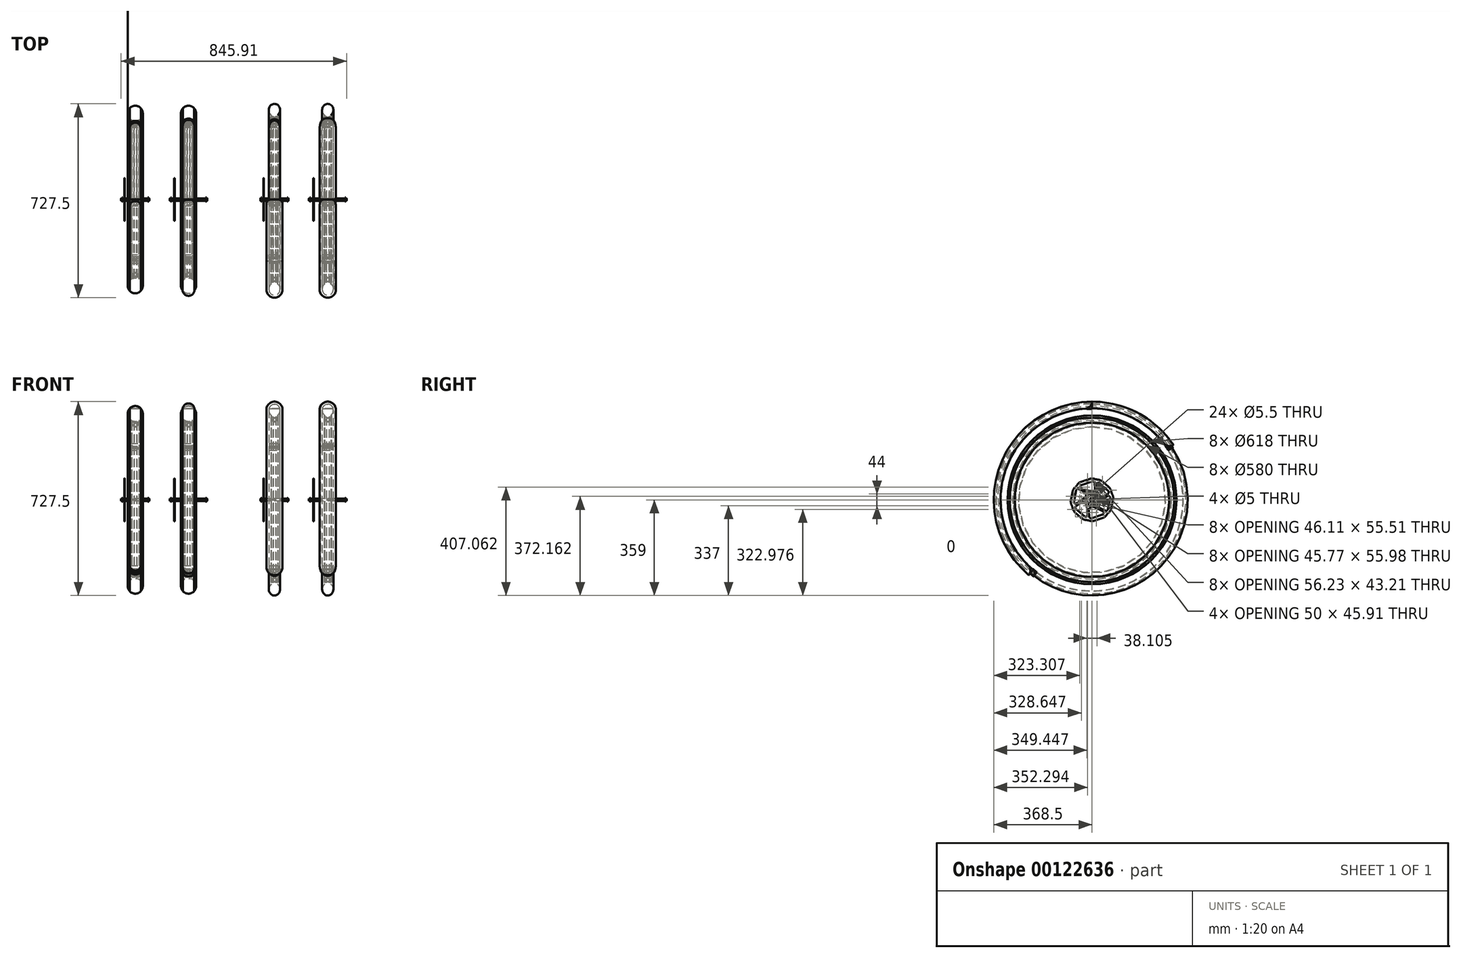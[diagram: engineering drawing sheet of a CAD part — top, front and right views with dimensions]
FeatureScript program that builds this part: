
annotation { "Feature Type Name" : "Feature", "Feature Type Description" : "" }
export const myFeature = defineFeature(function(context is Context, id is Id, definition is map)
    precondition{}
    {
        {
            var Q0;
            Q0=qCreatedBy(makeId("Front.planeOp"),FACE);
            var sketch = newSketch(context, id + "F0", { "sketchPlane" : qUnion([Q0])});
            skLineSegment(sketch, "E0.0", {"start": v(0, 313.27) * mm, "end": v(0, 0) * mm, "construction": true});
            skPoint(sketch, "E1.0", {"position": v(0, 0) * mm});
            skEllipticalArc(sketch, "E2", {});
            skLineSegment(sketch, "E3", {"start": v(-11.5, 309) * mm, "end": v(-5.5, 309) * mm});
            skArc(sketch, "E4", {"start": v(-5.5, 309) * mm, "mid": v(0, 306.5) * mm, "end": v(5.5, 309) * mm});
            skArc(sketch, "E5", {"start": v(-8.42, 300.83) * mm, "mid": v(0, 295) * mm, "end": v(8.42, 300.83) * mm});
            skLineSegment(sketch, "E6", {"start": v(-8.42, 300.83) * mm, "end": v(-11.5, 309) * mm});
            skLineSegment(sketch, "E7", {"start": v(5.5, 309) * mm, "end": v(11.5, 309) * mm});
            skLineSegment(sketch, "E8", {"start": v(11.5, 309) * mm, "end": v(8.42, 300.83) * mm});
            skLineSegment(sketch, "E9.1", {"start": v(4.5, 311) * mm, "end": v(11.5, 311) * mm});
            skArc(sketch, "E9.3", {"start": v(-4.5, 311) * mm, "mid": v(0, 308.5) * mm, "end": v(4.5, 311) * mm});
            skLineSegment(sketch, "E10", {"start": v(-11.5, 311) * mm, "end": v(-11.5, 317) * mm});
            skLineSegment(sketch, "E11", {"start": v(11.5, 311) * mm, "end": v(11.5, 317) * mm});
            skLineSegment(sketch, "E12.0", {"start": v(13.5, 308.64) * mm, "end": v(13.5, 317) * mm});
            skLineSegment(sketch, "E12.1", {"start": v(-13.5, 308.64) * mm, "end": v(-13.5, 317) * mm});
            skLineSegment(sketch, "E12.2", {"start": v(-10.3, 300.12) * mm, "end": v(-13.5, 308.64) * mm});
            skArc(sketch, "E12.3", {"start": v(-10.3, 300.12) * mm, "mid": v(0, 293) * mm, "end": v(10.3, 300.12) * mm});
            skLineSegment(sketch, "E12.4", {"start": v(13.5, 308.64) * mm, "end": v(10.3, 300.12) * mm});
            skLineSegment(sketch, "E13.trimOffspring", {"start": v(-11.5, 311) * mm, "end": v(-4.5, 311) * mm});
            skPoint(sketch, "E14", {"position": v(0, 308.5) * mm});
            skLineSegment(sketch, "E15", {"start": v(-11.5, 317) * mm, "end": v(-13.5, 317) * mm});
            skLineSegment(sketch, "E16", {"start": v(11.5, 317) * mm, "end": v(13.5, 317) * mm});
            skPoint(sketch, "E17", {"position": v(0, 295) * mm});
            skLineSegment(sketch, "E18", {"start": v(-21, 336.13) * mm, "end": v(21, 336.13) * mm, "construction": true});
            skPoint(sketch, "E19.orphan", {"position": v(0, 359) * mm});
            skLineSegment(sketch, "E20", {"start": v(-50, 7.5) * mm, "end": v(-50, 4.5) * mm});
            skPoint(sketch, "E21", {"position": v(53, 0) * mm});
            skPoint(sketch, "E22", {"position": v(-50, -7.5) * mm});
            skPoint(sketch, "E23", {"position": v(-47, 7.5) * mm});
            skPoint(sketch, "E24", {"position": v(-47, 4.5) * mm});
            skLineSegment(sketch, "E25", {"start": v(-50, 7.5) * mm, "end": v(-47, 7.5) * mm});
            skLineSegment(sketch, "E26", {"start": v(-47, 4.5) * mm, "end": v(-47, 7.5) * mm});
            skPoint(sketch, "E27.orphan", {"position": v(-50, 4.5) * mm});
            skLineSegment(sketch, "E28", {"start": v(-50, 4.5) * mm, "end": v(-53, 4.5) * mm});
            skLineSegment(sketch, "E29", {"start": v(-53, 4.5) * mm, "end": v(-53, 2.5) * mm});
            skLineSegment(sketch, "E30", {"start": v(0, 0) * mm, "end": v(53, 0) * mm, "construction": true});
            skPoint(sketch, "E31", {"position": v(-53, 2.5) * mm});
            skPoint(sketch, "E32.MirrorP", {"position": v(-53, -2.5) * mm});
            skPoint(sketch, "E33", {"position": v(-53, 4.5) * mm});
            skPoint(sketch, "E34.MirrorP", {"position": v(-53, -4.5) * mm});
            skLineSegment(sketch, "E35", {"start": v(-53, 2.5) * mm, "end": v(53, 2.5) * mm});
            skLineSegment(sketch, "E36", {"start": v(47, 4.5) * mm, "end": v(-47, 4.5) * mm});
            skArc(sketch, "E37", {"start": v(28.52, 343.23) * mm, "mid": v(0, 367) * mm, "end": v(-28.52, 343.23) * mm});
            skArc(sketch, "E38.0", {"start": v(30, 343.5) * mm, "mid": v(0, 368.5) * mm, "end": v(-30, 343.5) * mm});
            skLineSegment(sketch, "E39", {"start": v(-28.52, 343.23) * mm, "end": v(-30, 343.5) * mm});
            skLineSegment(sketch, "E40", {"start": v(28.52, 343.23) * mm, "end": v(30, 343.5) * mm});
            skPoint(sketch, "E41", {"position": v(0, 368.5) * mm});
            skPoint(sketch, "E42", {"position": v(0, 367) * mm});
            skPoint(sketch, "E43", {"position": v(-50, 7.5) * mm});
            skPoint(sketch, "E44.MirrorP", {"position": v(47, 7.5) * mm});
            skPoint(sketch, "E45.MirrorP", {"position": v(50, 7.5) * mm});
            skPoint(sketch, "E46.MirrorP", {"position": v(50, 4.5) * mm});
            skPoint(sketch, "E47.MirrorP", {"position": v(53, 4.5) * mm});
            skLineSegment(sketch, "E48", {"start": v(47, 4.5) * mm, "end": v(47, 7.5) * mm});
            skLineSegment(sketch, "E49", {"start": v(50, 7.5) * mm, "end": v(50, 4.5) * mm});
            skLineSegment(sketch, "E50", {"start": v(50, 7.5) * mm, "end": v(47, 7.5) * mm});
            skLineSegment(sketch, "E51", {"start": v(50, 4.5) * mm, "end": v(53, 4.5) * mm});
            skLineSegment(sketch, "E52", {"start": v(53, 4.5) * mm, "end": v(53, 2.5) * mm});
            skLineSegment(sketch, "E53.0", {"start": v(-522.41, 294.8) * mm, "end": v(-522.41, 0) * mm, "construction": true});
            skLineSegment(sketch, "E54", {"start": v(-535.91, 290) * mm, "end": v(-527.91, 290) * mm});
            skArc(sketch, "E55", {"start": v(-527.91, 290) * mm, "mid": v(-522.41, 287.5) * mm, "end": v(-516.91, 290) * mm});
            skArc(sketch, "E56", {"start": v(-530.13, 280.37) * mm, "mid": v(-522.41, 276) * mm, "end": v(-514.7, 280.37) * mm});
            skLineSegment(sketch, "E57", {"start": v(-530.13, 280.37) * mm, "end": v(-535.91, 290) * mm});
            skLineSegment(sketch, "E58", {"start": v(-516.91, 290) * mm, "end": v(-508.91, 290) * mm});
            skLineSegment(sketch, "E59", {"start": v(-508.91, 290) * mm, "end": v(-514.7, 280.37) * mm});
            skLineSegment(sketch, "E60.1", {"start": v(-517.91, 292) * mm, "end": v(-508.91, 292) * mm});
            skArc(sketch, "E60.3", {"start": v(-526.91, 292) * mm, "mid": v(-522.41, 289.5) * mm, "end": v(-517.91, 292) * mm});
            skLineSegment(sketch, "E61", {"start": v(-535.91, 292) * mm, "end": v(-535.91, 298) * mm});
            skLineSegment(sketch, "E62", {"start": v(-508.91, 292) * mm, "end": v(-508.91, 298) * mm});
            skLineSegment(sketch, "E63.0", {"start": v(-506.91, 289.45) * mm, "end": v(-506.91, 298) * mm});
            skLineSegment(sketch, "E63.1", {"start": v(-537.91, 289.45) * mm, "end": v(-537.91, 298) * mm});
            skLineSegment(sketch, "E63.2", {"start": v(-531.85, 279.34) * mm, "end": v(-537.91, 289.45) * mm});
            skArc(sketch, "E63.3", {"start": v(-531.85, 279.34) * mm, "mid": v(-522.41, 274) * mm, "end": v(-512.98, 279.34) * mm});
            skLineSegment(sketch, "E63.4", {"start": v(-506.91, 289.45) * mm, "end": v(-512.98, 279.34) * mm});
            skLineSegment(sketch, "E64.trimOffspring", {"start": v(-535.91, 292) * mm, "end": v(-526.91, 292) * mm});
            skPoint(sketch, "E65", {"position": v(-522.41, 289.5) * mm});
            skLineSegment(sketch, "E66", {"start": v(-535.91, 298) * mm, "end": v(-537.91, 298) * mm});
            skLineSegment(sketch, "E67", {"start": v(-508.91, 298) * mm, "end": v(-506.91, 298) * mm});
            skPoint(sketch, "E68", {"position": v(-522.41, 276) * mm});
            skPoint(sketch, "E69.orphan", {"position": v(-522.41, 352) * mm});
            skLineSegment(sketch, "E70", {"start": v(-522.41, 0) * mm, "end": v(-522.41, 0) * mm});
            skArc(sketch, "E71", {"start": v(-501.4, 341.32) * mm, "mid": v(-522.41, 360) * mm, "end": v(-543.42, 341.32) * mm});
            skArc(sketch, "E72.0", {"start": v(-499.91, 341.5) * mm, "mid": v(-522.41, 361.5) * mm, "end": v(-544.91, 341.5) * mm});
            skLineSegment(sketch, "E73", {"start": v(-543.42, 341.32) * mm, "end": v(-544.91, 341.5) * mm});
            skLineSegment(sketch, "E74", {"start": v(-501.4, 341.32) * mm, "end": v(-499.91, 341.5) * mm});
            skPoint(sketch, "E75", {"position": v(-522.41, 361.5) * mm});
            skPoint(sketch, "E76", {"position": v(-522.41, 360) * mm});
            skPoint(sketch, "E77.1.0.0", {"position": v(200, 367) * mm});
            skArc(sketch, "E77.1.0.1", {"start": v(230, 343.5) * mm, "mid": v(200, 368.5) * mm, "end": v(170, 343.5) * mm});
            skArc(sketch, "E77.1.0.2", {"start": v(228.52, 343.23) * mm, "mid": v(200, 367) * mm, "end": v(171.48, 343.23) * mm});
            skPoint(sketch, "E77.1.0.3", {"position": v(200, 368.5) * mm});
            skLineSegment(sketch, "E77.1.0.4", {"start": v(228.52, 343.23) * mm, "end": v(230, 343.5) * mm});
            skLineSegment(sketch, "E77.1.0.5", {"start": v(171.48, 343.23) * mm, "end": v(170, 343.5) * mm});
            skLineSegment(sketch, "E77.direction1", {"start": v(170, 343.5) * mm, "end": v(-30, 343.5) * mm, "construction": true});
            skArc(sketch, "E78.1.0.0", {"start": v(-301.4, 341.32) * mm, "mid": v(-322.41, 360) * mm, "end": v(-343.42, 341.32) * mm});
            skArc(sketch, "E78.1.0.1", {"start": v(-299.91, 341.5) * mm, "mid": v(-322.41, 361.5) * mm, "end": v(-344.91, 341.5) * mm});
            skPoint(sketch, "E78.1.0.2", {"position": v(-322.41, 360) * mm});
            skPoint(sketch, "E78.1.0.3", {"position": v(-322.41, 361.5) * mm});
            skLineSegment(sketch, "E78.1.0.4", {"start": v(-343.42, 341.32) * mm, "end": v(-344.91, 341.5) * mm});
            skLineSegment(sketch, "E78.1.0.5", {"start": v(-301.4, 341.32) * mm, "end": v(-299.91, 341.5) * mm});
            skLineSegment(sketch, "E78.direction1", {"start": v(-544.91, 341.5) * mm, "end": v(-344.91, 341.5) * mm, "construction": true});
            skPoint(sketch, "E79", {"position": v(-322.41, 0) * mm});
            skPoint(sketch, "E80", {"position": v(200, 0) * mm});
            skPoint(sketch, "E81", {"position": v(0, -359) * mm});
            skPoint(sketch, "E82", {"position": v(200, -359) * mm});
            skPoint(sketch, "E83", {"position": v(-522.41, -352) * mm});
            skPoint(sketch, "E84", {"position": v(-322.41, -352) * mm});
            skLineSegment(sketch, "E85", {"start": v(132.5, 7.5) * mm, "end": v(132.5, 4.5) * mm});
            skPoint(sketch, "E86", {"position": v(270.5, 0) * mm});
            skPoint(sketch, "E87", {"position": v(132.5, -7.5) * mm});
            skPoint(sketch, "E88", {"position": v(135.5, 7.5) * mm});
            skPoint(sketch, "E89", {"position": v(135.5, 4.5) * mm});
            skLineSegment(sketch, "E90", {"start": v(132.5, 7.5) * mm, "end": v(135.5, 7.5) * mm});
            skLineSegment(sketch, "E91", {"start": v(135.5, 4.5) * mm, "end": v(135.5, 7.5) * mm});
            skPoint(sketch, "E92.orphan", {"position": v(132.5, 4.5) * mm});
            skLineSegment(sketch, "E93", {"start": v(132.5, 4.5) * mm, "end": v(129.5, 4.5) * mm});
            skLineSegment(sketch, "E94", {"start": v(129.5, 4.5) * mm, "end": v(129.5, 2.5) * mm});
            skLineSegment(sketch, "E95", {"start": v(200, 0) * mm, "end": v(270.5, 0) * mm, "construction": true});
            skPoint(sketch, "E96", {"position": v(129.5, 2.5) * mm});
            skPoint(sketch, "E97.MirrorP", {"position": v(129.5, -2.5) * mm});
            skPoint(sketch, "E98", {"position": v(129.5, 4.5) * mm});
            skPoint(sketch, "E99.MirrorP", {"position": v(129.5, -4.5) * mm});
            skLineSegment(sketch, "E100", {"start": v(129.5, 2.5) * mm, "end": v(270.5, 2.5) * mm});
            skLineSegment(sketch, "E101", {"start": v(264.5, 4.5) * mm, "end": v(135.5, 4.5) * mm});
            skPoint(sketch, "E102", {"position": v(132.5, 7.5) * mm});
            skPoint(sketch, "E103.MirrorP", {"position": v(264.5, 7.5) * mm});
            skPoint(sketch, "E104.MirrorP", {"position": v(267.5, 7.5) * mm});
            skPoint(sketch, "E105.MirrorP", {"position": v(267.5, 4.5) * mm});
            skPoint(sketch, "E106.MirrorP", {"position": v(270.5, 4.5) * mm});
            skLineSegment(sketch, "E107", {"start": v(264.5, 4.5) * mm, "end": v(264.5, 7.5) * mm});
            skLineSegment(sketch, "E108", {"start": v(267.5, 7.5) * mm, "end": v(267.5, 4.5) * mm});
            skLineSegment(sketch, "E109", {"start": v(267.5, 7.5) * mm, "end": v(264.5, 7.5) * mm});
            skLineSegment(sketch, "E110", {"start": v(267.5, 4.5) * mm, "end": v(270.5, 4.5) * mm});
            skLineSegment(sketch, "E111", {"start": v(270.5, 4.5) * mm, "end": v(270.5, 2.5) * mm});
            skLineSegment(sketch, "E112", {"start": v(200, 338) * mm, "end": v(200, 0) * mm, "construction": true});
            skPoint(sketch, "E113", {"position": v(-550.91, 323.29) * mm});
            skPoint(sketch, "E114", {"position": v(-493.91, 323.29) * mm});
            skEllipse(sketch, "E115", {"center": v(-522.41, 323.29) * mm, "majorRadius": 28.71 * mm, "minorRadius": 28.5 * mm, "majorAxis": v(0, 1)});
            skPoint(sketch, "E116", {"position": v(-41.3, 80) * mm});
            skPoint(sketch, "E117", {"position": v(145.95, 80) * mm});
            skPoint(sketch, "E118", {"position": v(-41.3, -80) * mm});
            skPoint(sketch, "E119", {"position": v(145.95, -80) * mm});
            skPoint(sketch, "E120", {"position": v(-39.5, 80) * mm});
            skPoint(sketch, "E121", {"position": v(147.75, 80) * mm});
            const initialGuessF0  = {"E2": [0, 0.3361332472642005, 0, 1, 0.022866752735799457, 0.021, 3.7211086809856493, 2.5620766261939387]};
            skSetInitialGuess(sketch, initialGuessF0);
            skSolve(sketch);
        }
        {
            var Q0;
            Q0=makeQuery(id+"F0.imprint","IMPRINT",FACE,{"disambiguationData":[TD([[makeQuery(id+"F0.imprint","IMPRINT",EDGE,{"derivedFrom":sQuery(id+"F0.wireOp",EDGE,"E85")}),1.0]])]});
            var Q1;
            Q1=makeQuery(id+"F0.imprint","IMPRINT",FACE,{"disambiguationData":[TD([[makeQuery(id+"F0.imprint","IMPRINT",EDGE,{"derivedFrom":sQuery(id+"F0.wireOp",EDGE,"E20")}),1.0]])]});
            var Q2;
            Q2=makeQuery(id+"F0.imprint","IMPRINT",FACE,{"disambiguationData":[TD([[makeQuery(id+"F0.imprint","IMPRINT",EDGE,{"derivedFrom":sQuery(id+"F0.wireOp",EDGE,"E3")}),1.0]])]});
            var Q3;
            Q3=makeQuery(id+"F0.imprint","IMPRINT",FACE,{"disambiguationData":[TD([[makeQuery(id+"F0.imprint","IMPRINT",EDGE,{"derivedFrom":sQuery(id+"F0.wireOp",EDGE,"E2")}),1.0]])]});
            var Q4;
            Q4=makeQuery(id+"F0.imprint","IMPRINT",FACE,{"disambiguationData":[TD([[makeQuery(id+"F0.imprint","IMPRINT",EDGE,{"derivedFrom":sQuery(id+"F0.wireOp",EDGE,"E54")}),1.0]])]});
            var Q5;
            {var subQ0=sQuery(id+"F0.wireOp",EDGE,"E115");var subQ1=makeQuery(id+"F0.imprint","INTERSECT",VERTEX,{"derivedFrom":[sQuery(id+"F0.wireOp",EDGE,"E61"),sQuery(id+"F0.wireOp",EDGE,"E66"),subQ0]});Q5=makeQuery(id+"F0.imprint","IMPRINT",FACE,{"disambiguationData":[TD([[makeQuery(id+"F0.imprint","IMPRINT",EDGE,{"disambiguationData":[TD([[subQ1,-1.0]])],"derivedFrom":subQ0}),1.0]])]});}
            var Q6;
            Q6=sQuery(id+"F0.wireOp",EDGE,"E30");
            revolve(context, id + "F1", {"entities" : qUnion([Q0, Q1, Q2, Q3, Q4, Q5]), "axis" : qUnion([Q6]), "revolveType" : RevolveType.FULL});
        }
        {
            var Q0;
            Q0=makeQuery(id+"F0.imprint","IMPRINT",FACE,{"disambiguationData":[TD([[makeQuery(id+"F0.imprint","IMPRINT",EDGE,{"derivedFrom":sQuery(id+"F0.wireOp",EDGE,"E3")}),1.0]])]});
            var Q1;
            Q1=makeQuery(id+"F0.imprint","IMPRINT",FACE,{"disambiguationData":[TD([[makeQuery(id+"F0.imprint","IMPRINT",EDGE,{"derivedFrom":sQuery(id+"F0.wireOp",EDGE,"E54")}),1.0]])]});
            var Q2;
            Q2=sQuery(id+"F0.wireOp",EDGE,"E30");
            revolve(context, id + "F2", {"entities" : qUnion([Q0, Q1]), "axis" : qUnion([Q2]), "revolveType" : RevolveType.FULL});
        }
        {
            var Q0;
            Q0=sQuery(id+"F0.wireOp",VERTEX,"E116");
            var Q1;
            Q1=qCreatedBy(makeId("Right.planeOp"),FACE);
            cPlane(context, id + "F3", {"entities" : qUnion([Q0, Q1]), "cplaneType" : CPlaneType.PLANE_POINT, "offset" : 25 * mm, "width" : 150 * mm, "height" : 150 * mm});
        }
        {
            var Q0;
            Q0=qCreatedBy(id+"F3.planeOp",FACE);
            var sketch = newSketch(context, id + "F4", { "sketchPlane" : qUnion([Q0])});
            skPoint(sketch, "E122.0", {"position": v(0, 0) * mm});
            skCircle(sketch, "E123", {"center": v(0, 0) * mm, "radius": 80 * mm, "construction": true});
            skCircle(sketch, "E124", {"center": v(0, 0) * mm, "radius": 17.4 * mm, "construction": true});
            skCircle(sketch, "E125", {"center": v(0, 22) * mm, "radius": 2.75 * mm});
            skCircle(sketch, "E126.1.0", {"center": v(-19.05, 11) * mm, "radius": 2.75 * mm});
            skCircle(sketch, "E126.2.0", {"center": v(-19.05, -11) * mm, "radius": 2.75 * mm});
            skCircle(sketch, "E126.3.0", {"center": v(0, -22) * mm, "radius": 2.75 * mm});
            skCircle(sketch, "E126.4.0", {"center": v(19.05, -11) * mm, "radius": 2.75 * mm});
            skCircle(sketch, "E126.5.0", {"center": v(19.05, 11) * mm, "radius": 2.75 * mm});
            skArc(sketch, "E127", {"start": v(-62.27, 48.24) * mm, "mid": v(-66.15, 44.44) * mm, "end": v(-69.28, 40) * mm});
            skArc(sketch, "E128", {"start": v(-62.27, 48.24) * mm, "mid": v(-58.71, 51.67) * mm, "end": v(-55.77, 55.63) * mm});
            skArc(sketch, "E129", {"start": v(-48.48, 63.64) * mm, "mid": v(-52.49, 59.97) * mm, "end": v(-55.77, 55.63) * mm});
            skLineSegment(sketch, "E130", {"start": v(0, 0) * mm, "end": v(-69.28, 40) * mm, "construction": true});
            skArc(sketch, "E131", {"start": v(-39.9, 68.2) * mm, "mid": v(-44.37, 66.27) * mm, "end": v(-48.48, 63.64) * mm});
            skLineSegment(sketch, "E132", {"start": v(0, 0) * mm, "end": v(0, 80) * mm, "construction": true});
            skArc(sketch, "E133", {"start": v(0, 80) * mm, "mid": v(-4.86, 79.6) * mm, "end": v(-9.6, 78.42) * mm});
            skLineSegment(sketch, "E134", {"start": v(-9.6, 78.42) * mm, "end": v(-39.9, 68.2) * mm});
            skLineSegment(sketch, "E135", {"start": v(-39.57, 55.64) * mm, "end": v(1, 69.33) * mm});
            skArc(sketch, "E136", {"start": v(-39.57, 55.64) * mm, "mid": v(-44.32, 49.42) * mm, "end": v(-40.34, 42.68) * mm});
            skLineSegment(sketch, "E137", {"start": v(-40.34, 42.68) * mm, "end": v(-9, 27.82) * mm});
            skArc(sketch, "E138", {"start": v(-9, 27.82) * mm, "mid": v(5.62, 29) * mm, "end": v(11.91, 42.27) * mm});
            skArc(sketch, "E139", {"start": v(10.21, 63.27) * mm, "mid": v(7.09, 68.55) * mm, "end": v(1, 69.33) * mm});
            skLineSegment(sketch, "E140", {"start": v(11.91, 42.27) * mm, "end": v(10.21, 63.27) * mm});
            skArc(sketch, "E141", {"start": v(13.84, 18.34) * mm, "mid": v(9.67, 22.93) * mm, "end": v(4.17, 20.07) * mm});
            skLineSegment(sketch, "E142.1.0", {"start": v(-67.97, -6.45) * mm, "end": v(-59.55, 35.53) * mm});
            skArc(sketch, "E142.1.1", {"start": v(-67.97, -6.45) * mm, "mid": v(-64.96, -13.68) * mm, "end": v(-57.13, -13.59) * mm});
            skLineSegment(sketch, "E142.1.2", {"start": v(-57.13, -13.59) * mm, "end": v(-28.6, 6.1) * mm});
            skArc(sketch, "E142.1.3", {"start": v(-28.6, 6.1) * mm, "mid": v(-22.31, 19.37) * mm, "end": v(-30.65, 31.45) * mm});
            skLineSegment(sketch, "E142.1.4", {"start": v(-30.65, 31.45) * mm, "end": v(-49.68, 40.48) * mm});
            skArc(sketch, "E142.1.5", {"start": v(-49.68, 40.48) * mm, "mid": v(-55.82, 40.41) * mm, "end": v(-59.55, 35.53) * mm});
            skLineSegment(sketch, "E142.2.0", {"start": v(-28.4, -62.1) * mm, "end": v(-60.54, -33.8) * mm});
            skArc(sketch, "E142.2.1", {"start": v(-28.4, -62.1) * mm, "mid": v(-20.64, -63.1) * mm, "end": v(-16.8, -56.27) * mm});
            skLineSegment(sketch, "E142.2.2", {"start": v(-16.8, -56.27) * mm, "end": v(-19.6, -21.71) * mm});
            skArc(sketch, "E142.2.3", {"start": v(-19.6, -21.71) * mm, "mid": v(-27.93, -9.64) * mm, "end": v(-42.56, -10.82) * mm});
            skLineSegment(sketch, "E142.2.4", {"start": v(-42.56, -10.82) * mm, "end": v(-59.9, -22.79) * mm});
            skArc(sketch, "E142.2.5", {"start": v(-59.9, -22.79) * mm, "mid": v(-62.9, -28.14) * mm, "end": v(-60.54, -33.8) * mm});
            skLineSegment(sketch, "E142.3.0", {"start": v(39.57, -55.64) * mm, "end": v(-1, -69.33) * mm});
            skArc(sketch, "E142.3.1", {"start": v(39.57, -55.64) * mm, "mid": v(44.32, -49.42) * mm, "end": v(40.34, -42.68) * mm});
            skLineSegment(sketch, "E142.3.2", {"start": v(40.34, -42.68) * mm, "end": v(9, -27.82) * mm});
            skArc(sketch, "E142.3.3", {"start": v(9, -27.82) * mm, "mid": v(-5.62, -29) * mm, "end": v(-11.91, -42.27) * mm});
            skLineSegment(sketch, "E142.3.4", {"start": v(-11.91, -42.27) * mm, "end": v(-10.21, -63.27) * mm});
            skArc(sketch, "E142.3.5", {"start": v(-10.21, -63.27) * mm, "mid": v(-7.09, -68.55) * mm, "end": v(-1, -69.33) * mm});
            skLineSegment(sketch, "E142.4.0", {"start": v(67.97, 6.45) * mm, "end": v(59.55, -35.53) * mm});
            skArc(sketch, "E142.4.1", {"start": v(67.97, 6.45) * mm, "mid": v(64.96, 13.68) * mm, "end": v(57.13, 13.59) * mm});
            skLineSegment(sketch, "E142.4.2", {"start": v(57.13, 13.59) * mm, "end": v(28.6, -6.1) * mm});
            skArc(sketch, "E142.4.3", {"start": v(28.6, -6.1) * mm, "mid": v(22.31, -19.37) * mm, "end": v(30.65, -31.45) * mm});
            skLineSegment(sketch, "E142.4.4", {"start": v(30.65, -31.45) * mm, "end": v(49.68, -40.48) * mm});
            skArc(sketch, "E142.4.5", {"start": v(49.68, -40.48) * mm, "mid": v(55.82, -40.41) * mm, "end": v(59.55, -35.53) * mm});
            skLineSegment(sketch, "E142.5.0", {"start": v(28.4, 62.1) * mm, "end": v(60.54, 33.8) * mm});
            skArc(sketch, "E142.5.1", {"start": v(28.4, 62.1) * mm, "mid": v(20.64, 63.1) * mm, "end": v(16.8, 56.27) * mm});
            skLineSegment(sketch, "E142.5.2", {"start": v(16.8, 56.27) * mm, "end": v(19.6, 21.71) * mm});
            skArc(sketch, "E142.5.3", {"start": v(19.6, 21.71) * mm, "mid": v(27.93, 9.64) * mm, "end": v(42.56, 10.82) * mm});
            skLineSegment(sketch, "E142.5.4", {"start": v(42.56, 10.82) * mm, "end": v(59.9, 22.79) * mm});
            skArc(sketch, "E142.5.5", {"start": v(59.9, 22.79) * mm, "mid": v(62.9, 28.14) * mm, "end": v(60.54, 33.8) * mm});
            skLineSegment(sketch, "E143", {"start": v(-1.97, 17.84) * mm, "end": v(-8.96, 21.16) * mm});
            skLineSegment(sketch, "E144.1.0", {"start": v(-16.44, 7.21) * mm, "end": v(-22.8, 2.82) * mm});
            skArc(sketch, "E144.1.1", {"start": v(-16.44, 7.21) * mm, "mid": v(-14.52, 10.2) * mm, "end": v(-15.3, 13.65) * mm});
            skArc(sketch, "E144.1.2", {"start": v(-8.96, 21.16) * mm, "mid": v(-15.02, 19.84) * mm, "end": v(-15.3, 13.65) * mm});
            skLineSegment(sketch, "E144.2.0", {"start": v(-14.47, -10.63) * mm, "end": v(-13.84, -18.34) * mm});
            skArc(sketch, "E144.2.1", {"start": v(-14.47, -10.63) * mm, "mid": v(-16.09, -7.48) * mm, "end": v(-19.47, -6.42) * mm});
            skArc(sketch, "E144.2.2", {"start": v(-22.8, 2.82) * mm, "mid": v(-24.7, -3.09) * mm, "end": v(-19.47, -6.42) * mm});
            skLineSegment(sketch, "E144.3.0", {"start": v(1.97, -17.84) * mm, "end": v(8.96, -21.16) * mm});
            skArc(sketch, "E144.3.1", {"start": v(1.97, -17.84) * mm, "mid": v(-1.56, -17.67) * mm, "end": v(-4.17, -20.07) * mm});
            skArc(sketch, "E144.3.2", {"start": v(-13.84, -18.34) * mm, "mid": v(-9.67, -22.93) * mm, "end": v(-4.17, -20.07) * mm});
            skLineSegment(sketch, "E144.4.0", {"start": v(16.44, -7.21) * mm, "end": v(22.8, -2.82) * mm});
            skArc(sketch, "E144.4.1", {"start": v(16.44, -7.21) * mm, "mid": v(14.52, -10.2) * mm, "end": v(15.3, -13.65) * mm});
            skArc(sketch, "E144.4.2", {"start": v(8.96, -21.16) * mm, "mid": v(15.02, -19.84) * mm, "end": v(15.3, -13.65) * mm});
            skLineSegment(sketch, "E144.5.0", {"start": v(14.47, 10.63) * mm, "end": v(13.84, 18.34) * mm});
            skArc(sketch, "E144.5.1", {"start": v(14.47, 10.63) * mm, "mid": v(16.09, 7.48) * mm, "end": v(19.47, 6.42) * mm});
            skArc(sketch, "E144.5.2", {"start": v(22.8, -2.82) * mm, "mid": v(24.7, 3.09) * mm, "end": v(19.47, 6.42) * mm});
            skArc(sketch, "E145", {"start": v(4.17, 20.07) * mm, "mid": v(-1.56, 26.33) * mm, "end": v(-1.97, 17.84) * mm, "construction": true});
            skArc(sketch, "E146", {"start": v(-1.97, 17.84) * mm, "mid": v(1.56, 17.67) * mm, "end": v(4.17, 20.07) * mm});
            skLineSegment(sketch, "E147", {"start": v(0, 0) * mm, "end": v(-30.3, 39.77) * mm, "construction": true});
            skLineSegment(sketch, "E148.1.0", {"start": v(-72.71, 30.9) * mm, "end": v(-79, -0.45) * mm});
            skArc(sketch, "E148.1.1", {"start": v(-69.28, 40) * mm, "mid": v(-71.37, 35.6) * mm, "end": v(-72.71, 30.9) * mm});
            skArc(sketch, "E148.1.2", {"start": v(-79, -0.45) * mm, "mid": v(-79.58, -5.3) * mm, "end": v(-79.35, -10.17) * mm});
            skArc(sketch, "E148.1.3", {"start": v(-79.35, -10.17) * mm, "mid": v(-78.18, -15.47) * mm, "end": v(-76.06, -20.48) * mm});
            skArc(sketch, "E148.1.4", {"start": v(-72.91, -29.8) * mm, "mid": v(-74.1, -25.01) * mm, "end": v(-76.06, -20.48) * mm});
            skArc(sketch, "E148.1.5", {"start": v(-72.91, -29.8) * mm, "mid": v(-71.56, -35.07) * mm, "end": v(-69.28, -40) * mm});
            skLineSegment(sketch, "E148.2.0", {"start": v(-63.12, -47.52) * mm, "end": v(-39.11, -68.65) * mm});
            skArc(sketch, "E148.2.1", {"start": v(-69.28, -40) * mm, "mid": v(-66.5, -44.01) * mm, "end": v(-63.12, -47.52) * mm});
            skArc(sketch, "E148.2.2", {"start": v(-39.11, -68.65) * mm, "mid": v(-35.2, -71.56) * mm, "end": v(-30.87, -73.8) * mm});
            skArc(sketch, "E148.2.3", {"start": v(-30.87, -73.8) * mm, "mid": v(-25.69, -75.44) * mm, "end": v(-20.3, -76.11) * mm});
            skArc(sketch, "E148.2.4", {"start": v(-10.65, -78.05) * mm, "mid": v(-15.4, -76.68) * mm, "end": v(-20.3, -76.11) * mm});
            skArc(sketch, "E148.2.5", {"start": v(-10.65, -78.05) * mm, "mid": v(-5.41, -79.5) * mm, "end": v(0, -80) * mm});
            skLineSegment(sketch, "E148.3.0", {"start": v(9.6, -78.42) * mm, "end": v(39.9, -68.2) * mm});
            skArc(sketch, "E148.3.1", {"start": v(0, -80) * mm, "mid": v(4.86, -79.6) * mm, "end": v(9.6, -78.42) * mm});
            skArc(sketch, "E148.3.2", {"start": v(39.9, -68.2) * mm, "mid": v(44.37, -66.27) * mm, "end": v(48.48, -63.64) * mm});
            skArc(sketch, "E148.3.3", {"start": v(48.48, -63.64) * mm, "mid": v(52.49, -59.97) * mm, "end": v(55.77, -55.63) * mm});
            skArc(sketch, "E148.3.4", {"start": v(62.27, -48.24) * mm, "mid": v(58.71, -51.67) * mm, "end": v(55.77, -55.63) * mm});
            skArc(sketch, "E148.3.5", {"start": v(62.27, -48.24) * mm, "mid": v(66.15, -44.44) * mm, "end": v(69.28, -40) * mm});
            skLineSegment(sketch, "E148.4.0", {"start": v(72.71, -30.9) * mm, "end": v(79, 0.45) * mm});
            skArc(sketch, "E148.4.1", {"start": v(69.28, -40) * mm, "mid": v(71.37, -35.6) * mm, "end": v(72.71, -30.9) * mm});
            skArc(sketch, "E148.4.2", {"start": v(79, 0.45) * mm, "mid": v(79.58, 5.3) * mm, "end": v(79.35, 10.17) * mm});
            skArc(sketch, "E148.4.3", {"start": v(79.35, 10.17) * mm, "mid": v(78.18, 15.47) * mm, "end": v(76.06, 20.48) * mm});
            skArc(sketch, "E148.4.4", {"start": v(72.91, 29.8) * mm, "mid": v(74.1, 25.01) * mm, "end": v(76.06, 20.48) * mm});
            skArc(sketch, "E148.4.5", {"start": v(72.91, 29.8) * mm, "mid": v(71.56, 35.07) * mm, "end": v(69.28, 40) * mm});
            skLineSegment(sketch, "E148.5.0", {"start": v(63.12, 47.52) * mm, "end": v(39.11, 68.65) * mm});
            skArc(sketch, "E148.5.1", {"start": v(69.28, 40) * mm, "mid": v(66.5, 44.01) * mm, "end": v(63.12, 47.52) * mm});
            skArc(sketch, "E148.5.2", {"start": v(39.11, 68.65) * mm, "mid": v(35.2, 71.56) * mm, "end": v(30.87, 73.8) * mm});
            skArc(sketch, "E148.5.3", {"start": v(30.87, 73.8) * mm, "mid": v(25.69, 75.44) * mm, "end": v(20.3, 76.11) * mm});
            skArc(sketch, "E148.5.4", {"start": v(10.65, 78.05) * mm, "mid": v(15.4, 76.68) * mm, "end": v(20.3, 76.11) * mm});
            skArc(sketch, "E148.5.5", {"start": v(10.65, 78.05) * mm, "mid": v(5.41, 79.5) * mm, "end": v(0, 80) * mm});
            skLineSegment(sketch, "E149", {"start": v(6.52, 22.48) * mm, "end": v(3.81, 27.94) * mm, "construction": true});
            skSolve(sketch);
        }
        {
            var Q0;
            Q0=makeQuery(id+"F4.imprint","IMPRINT",FACE,{"disambiguationData":[TD([[makeQuery(id+"F4.imprint","IMPRINT",EDGE,{"derivedFrom":sQuery(id+"F4.wireOp",EDGE,"E125")}),-1.0]])]});
            var Q1;
            Q1=sQuery(id+"F0.wireOp",VERTEX,"E120");
            extrude(context, id + "F5", {"entities" : qUnion([Q0]), "endBound" : BoundingType.UP_TO_VERTEX, "endBoundEntityVertex" : qUnion([Q1]), "depth" : 25 * mm});
        }
        {
            var Q0;
            Q0 = qSketchRegion(id + "F4", true);
            var Q1;
            Q1=sQuery(id+"F0.wireOp",VERTEX,"E121");
            var Q2;
            Q2=sQuery(id+"F0.wireOp",VERTEX,"E117");
            extrude(context, id + "F6", {"entities" : qUnion([Q0]), "endBound" : BoundingType.UP_TO_VERTEX, "endBoundEntityVertex" : qUnion([Q1]), "depth" : 25 * mm, "hasSecondDirection" : true, "secondDirectionBound" : SecondDirectionBoundingType.UP_TO_VERTEX, "secondDirectionOppositeDirection" : false, "secondDirectionBoundEntityVertex" : qUnion([Q2]), "secondDirectionDepth" : 25 * mm});
        }
        {
            var Q0;
            Q0=makeQuery(id+"F1.opRevolve","SWEPT_BODY",BODY,{"disambiguationData":[OSD([sQuery(id+"F0.wireOp",EDGE,"E2"),sQuery(id+"F0.wireOp",EDGE,"E9.1"),sQuery(id+"F0.wireOp",EDGE,"E9.3"),sQuery(id+"F0.wireOp",EDGE,"E10"),sQuery(id+"F0.wireOp",EDGE,"E11"),sQuery(id+"F0.wireOp",EDGE,"E13.trimOffspring")])]});
            var Q1;
            Q1=makeQuery(id+"F2.opRevolve","SWEPT_BODY",BODY,{"disambiguationData":[OSD([sQuery(id+"F0.wireOp",EDGE,"E3"),sQuery(id+"F0.wireOp",EDGE,"E4"),sQuery(id+"F0.wireOp",EDGE,"E5"),sQuery(id+"F0.wireOp",EDGE,"E6"),sQuery(id+"F0.wireOp",EDGE,"E7"),sQuery(id+"F0.wireOp",EDGE,"E8"),sQuery(id+"F0.wireOp",EDGE,"E9.1"),sQuery(id+"F0.wireOp",EDGE,"E9.3"),sQuery(id+"F0.wireOp",EDGE,"E10"),sQuery(id+"F0.wireOp",EDGE,"E11"),sQuery(id+"F0.wireOp",EDGE,"E12.0"),sQuery(id+"F0.wireOp",EDGE,"E12.1"),sQuery(id+"F0.wireOp",EDGE,"E12.2"),sQuery(id+"F0.wireOp",EDGE,"E12.3"),sQuery(id+"F0.wireOp",EDGE,"E12.4"),sQuery(id+"F0.wireOp",EDGE,"E13.trimOffspring"),sQuery(id+"F0.wireOp",EDGE,"E15"),sQuery(id+"F0.wireOp",EDGE,"E16")])]});
            var Q2;
            Q2=makeQuery(id+"F1.opRevolve","SWEPT_BODY",BODY,{"disambiguationData":[OSD([sQuery(id+"F0.wireOp",EDGE,"1e94019a-f873-4326-8328-37ccba4a5ada"),sQuery(id+"F0.wireOp",EDGE,"E60.1"),sQuery(id+"F0.wireOp",EDGE,"E60.3"),sQuery(id+"F0.wireOp",EDGE,"E61"),sQuery(id+"F0.wireOp",EDGE,"E62"),sQuery(id+"F0.wireOp",EDGE,"E64.trimOffspring")])]});
            var Q3;
            Q3=makeQuery(id+"F2.opRevolve","SWEPT_BODY",BODY,{"disambiguationData":[OSD([sQuery(id+"F0.wireOp",EDGE,"E54"),sQuery(id+"F0.wireOp",EDGE,"E55"),sQuery(id+"F0.wireOp",EDGE,"E56"),sQuery(id+"F0.wireOp",EDGE,"E57"),sQuery(id+"F0.wireOp",EDGE,"E58"),sQuery(id+"F0.wireOp",EDGE,"E59"),sQuery(id+"F0.wireOp",EDGE,"E60.1"),sQuery(id+"F0.wireOp",EDGE,"E60.3"),sQuery(id+"F0.wireOp",EDGE,"E61"),sQuery(id+"F0.wireOp",EDGE,"E62"),sQuery(id+"F0.wireOp",EDGE,"E63.0"),sQuery(id+"F0.wireOp",EDGE,"E63.1"),sQuery(id+"F0.wireOp",EDGE,"E63.2"),sQuery(id+"F0.wireOp",EDGE,"E63.3"),sQuery(id+"F0.wireOp",EDGE,"E63.4"),sQuery(id+"F0.wireOp",EDGE,"E64.trimOffspring"),sQuery(id+"F0.wireOp",EDGE,"E66"),sQuery(id+"F0.wireOp",EDGE,"E67")])]});
            var Q4;
            Q4=makeQuery(id+"F1.opRevolve","SWEPT_BODY",BODY,{"disambiguationData":[OSD([sQuery(id+"F0.wireOp",EDGE,"E115")])]});
            var Q5;
            Q5=sQuery(id+"F0.wireOp",VERTEX,"E53.0.end");
            var Q6;
            Q6=sQuery(id+"F0.wireOp",VERTEX,"E79");
            transform(context, id + "F7", {"entities" : qUnion([Q0, Q1, Q2, Q3, Q4]), "transformType" : TransformType.TRANSLATION_ENTITY, "oppositeDirectionEntity" : false, "transformLine" : qUnion([Q5, Q6]), "makeCopy" : true});
        }
        {
            var Q0;
            Q0=makeQuery(id+"F1.opRevolve","SWEPT_BODY",BODY,{"disambiguationData":[OSD([sQuery(id+"F0.wireOp",EDGE,"E85"),sQuery(id+"F0.wireOp",EDGE,"E90"),sQuery(id+"F0.wireOp",EDGE,"E91"),sQuery(id+"F0.wireOp",EDGE,"E93"),sQuery(id+"F0.wireOp",EDGE,"E94"),sQuery(id+"F0.wireOp",EDGE,"E100"),sQuery(id+"F0.wireOp",EDGE,"E101"),sQuery(id+"F0.wireOp",EDGE,"E107"),sQuery(id+"F0.wireOp",EDGE,"E108"),sQuery(id+"F0.wireOp",EDGE,"E109"),sQuery(id+"F0.wireOp",EDGE,"E110"),sQuery(id+"F0.wireOp",EDGE,"E111")])]});
            var Q1;
            Q1=makeQuery(id+"F1.opRevolve","SWEPT_BODY",BODY,{"disambiguationData":[OSD([sQuery(id+"F0.wireOp",EDGE,"E20"),sQuery(id+"F0.wireOp",EDGE,"E25"),sQuery(id+"F0.wireOp",EDGE,"E26"),sQuery(id+"F0.wireOp",EDGE,"E28"),sQuery(id+"F0.wireOp",EDGE,"E29"),sQuery(id+"F0.wireOp",EDGE,"E35"),sQuery(id+"F0.wireOp",EDGE,"E36"),sQuery(id+"F0.wireOp",EDGE,"E48"),sQuery(id+"F0.wireOp",EDGE,"E49"),sQuery(id+"F0.wireOp",EDGE,"E50"),sQuery(id+"F0.wireOp",EDGE,"E51"),sQuery(id+"F0.wireOp",EDGE,"E52")])]});
            var Q2;
            Q2=makeQuery(id+"F5.opExtrude","SWEPT_BODY",BODY,{"disambiguationData":[OSD([sQuery(id+"F4.wireOp",EDGE,"E125"),sQuery(id+"F4.wireOp",EDGE,"E126.1.0"),sQuery(id+"F4.wireOp",EDGE,"E126.2.0"),sQuery(id+"F4.wireOp",EDGE,"E126.3.0"),sQuery(id+"F4.wireOp",EDGE,"E126.4.0"),sQuery(id+"F4.wireOp",EDGE,"E126.5.0"),sQuery(id+"F4.wireOp",EDGE,"E127"),sQuery(id+"F4.wireOp",EDGE,"E128"),sQuery(id+"F4.wireOp",EDGE,"E129"),sQuery(id+"F4.wireOp",EDGE,"E131"),sQuery(id+"F4.wireOp",EDGE,"E133"),sQuery(id+"F4.wireOp",EDGE,"E134"),sQuery(id+"F4.wireOp",EDGE,"E135"),sQuery(id+"F4.wireOp",EDGE,"E136"),sQuery(id+"F4.wireOp",EDGE,"E137"),sQuery(id+"F4.wireOp",EDGE,"E138"),sQuery(id+"F4.wireOp",EDGE,"E139"),sQuery(id+"F4.wireOp",EDGE,"E140"),sQuery(id+"F4.wireOp",EDGE,"E141"),sQuery(id+"F4.wireOp",EDGE,"E142.1.0"),sQuery(id+"F4.wireOp",EDGE,"E142.1.1"),sQuery(id+"F4.wireOp",EDGE,"E142.1.2"),sQuery(id+"F4.wireOp",EDGE,"E142.1.3"),sQuery(id+"F4.wireOp",EDGE,"E142.1.4"),sQuery(id+"F4.wireOp",EDGE,"E142.1.5"),sQuery(id+"F4.wireOp",EDGE,"E142.2.0"),sQuery(id+"F4.wireOp",EDGE,"E142.2.1"),sQuery(id+"F4.wireOp",EDGE,"E142.2.2"),sQuery(id+"F4.wireOp",EDGE,"E142.2.3"),sQuery(id+"F4.wireOp",EDGE,"E142.2.4"),sQuery(id+"F4.wireOp",EDGE,"E142.2.5"),sQuery(id+"F4.wireOp",EDGE,"E142.3.0"),sQuery(id+"F4.wireOp",EDGE,"E142.3.1"),sQuery(id+"F4.wireOp",EDGE,"E142.3.2"),sQuery(id+"F4.wireOp",EDGE,"E142.3.3"),sQuery(id+"F4.wireOp",EDGE,"E142.3.4"),sQuery(id+"F4.wireOp",EDGE,"E142.3.5"),sQuery(id+"F4.wireOp",EDGE,"E142.4.0"),sQuery(id+"F4.wireOp",EDGE,"E142.4.1"),sQuery(id+"F4.wireOp",EDGE,"E142.4.2"),sQuery(id+"F4.wireOp",EDGE,"E142.4.3"),sQuery(id+"F4.wireOp",EDGE,"E142.4.4"),sQuery(id+"F4.wireOp",EDGE,"E142.4.5"),sQuery(id+"F4.wireOp",EDGE,"E142.5.0"),sQuery(id+"F4.wireOp",EDGE,"E142.5.1"),sQuery(id+"F4.wireOp",EDGE,"E142.5.2"),sQuery(id+"F4.wireOp",EDGE,"E142.5.3"),sQuery(id+"F4.wireOp",EDGE,"E142.5.4"),sQuery(id+"F4.wireOp",EDGE,"E142.5.5"),sQuery(id+"F4.wireOp",EDGE,"E143"),sQuery(id+"F4.wireOp",EDGE,"E144.1.0"),sQuery(id+"F4.wireOp",EDGE,"E144.1.1"),sQuery(id+"F4.wireOp",EDGE,"E144.1.2"),sQuery(id+"F4.wireOp",EDGE,"E144.2.0"),sQuery(id+"F4.wireOp",EDGE,"E144.2.1"),sQuery(id+"F4.wireOp",EDGE,"E144.2.2"),sQuery(id+"F4.wireOp",EDGE,"E144.3.0"),sQuery(id+"F4.wireOp",EDGE,"E144.3.1"),sQuery(id+"F4.wireOp",EDGE,"E144.3.2"),sQuery(id+"F4.wireOp",EDGE,"E144.4.0"),sQuery(id+"F4.wireOp",EDGE,"E144.4.1"),sQuery(id+"F4.wireOp",EDGE,"E144.4.2"),sQuery(id+"F4.wireOp",EDGE,"E144.5.0"),sQuery(id+"F4.wireOp",EDGE,"E144.5.1"),sQuery(id+"F4.wireOp",EDGE,"E144.5.2"),sQuery(id+"F4.wireOp",EDGE,"E146"),sQuery(id+"F4.wireOp",EDGE,"E148.1.0"),sQuery(id+"F4.wireOp",EDGE,"E148.1.1"),sQuery(id+"F4.wireOp",EDGE,"E148.1.2"),sQuery(id+"F4.wireOp",EDGE,"E148.1.3"),sQuery(id+"F4.wireOp",EDGE,"E148.1.4"),sQuery(id+"F4.wireOp",EDGE,"E148.1.5"),sQuery(id+"F4.wireOp",EDGE,"E148.2.0"),sQuery(id+"F4.wireOp",EDGE,"E148.2.1"),sQuery(id+"F4.wireOp",EDGE,"E148.2.2"),sQuery(id+"F4.wireOp",EDGE,"E148.2.3"),sQuery(id+"F4.wireOp",EDGE,"E148.2.4"),sQuery(id+"F4.wireOp",EDGE,"E148.2.5"),sQuery(id+"F4.wireOp",EDGE,"E148.3.0"),sQuery(id+"F4.wireOp",EDGE,"E148.3.1"),sQuery(id+"F4.wireOp",EDGE,"E148.3.2"),sQuery(id+"F4.wireOp",EDGE,"E148.3.3"),sQuery(id+"F4.wireOp",EDGE,"E148.3.4"),sQuery(id+"F4.wireOp",EDGE,"E148.3.5"),sQuery(id+"F4.wireOp",EDGE,"E148.4.0"),sQuery(id+"F4.wireOp",EDGE,"E148.4.1"),sQuery(id+"F4.wireOp",EDGE,"E148.4.2"),sQuery(id+"F4.wireOp",EDGE,"E148.4.3"),sQuery(id+"F4.wireOp",EDGE,"E148.4.4"),sQuery(id+"F4.wireOp",EDGE,"E148.4.5"),sQuery(id+"F4.wireOp",EDGE,"E148.5.0"),sQuery(id+"F4.wireOp",EDGE,"E148.5.1"),sQuery(id+"F4.wireOp",EDGE,"E148.5.2"),sQuery(id+"F4.wireOp",EDGE,"E148.5.3"),sQuery(id+"F4.wireOp",EDGE,"E148.5.4"),sQuery(id+"F4.wireOp",EDGE,"E148.5.5")])]});
            var Q3;
            Q3=makeQuery(id+"F6.opExtrude","SWEPT_BODY",BODY,{"disambiguationData":[OSD([sQuery(id+"F4.wireOp",EDGE,"E125"),sQuery(id+"F4.wireOp",EDGE,"E126.1.0"),sQuery(id+"F4.wireOp",EDGE,"E126.2.0"),sQuery(id+"F4.wireOp",EDGE,"E126.3.0"),sQuery(id+"F4.wireOp",EDGE,"E126.4.0"),sQuery(id+"F4.wireOp",EDGE,"E126.5.0"),sQuery(id+"F4.wireOp",EDGE,"E127"),sQuery(id+"F4.wireOp",EDGE,"E128"),sQuery(id+"F4.wireOp",EDGE,"E129"),sQuery(id+"F4.wireOp",EDGE,"E131"),sQuery(id+"F4.wireOp",EDGE,"E133"),sQuery(id+"F4.wireOp",EDGE,"E134"),sQuery(id+"F4.wireOp",EDGE,"E135"),sQuery(id+"F4.wireOp",EDGE,"E136"),sQuery(id+"F4.wireOp",EDGE,"E137"),sQuery(id+"F4.wireOp",EDGE,"E138"),sQuery(id+"F4.wireOp",EDGE,"E139"),sQuery(id+"F4.wireOp",EDGE,"E140"),sQuery(id+"F4.wireOp",EDGE,"E141"),sQuery(id+"F4.wireOp",EDGE,"E142.1.0"),sQuery(id+"F4.wireOp",EDGE,"E142.1.1"),sQuery(id+"F4.wireOp",EDGE,"E142.1.2"),sQuery(id+"F4.wireOp",EDGE,"E142.1.3"),sQuery(id+"F4.wireOp",EDGE,"E142.1.4"),sQuery(id+"F4.wireOp",EDGE,"E142.1.5"),sQuery(id+"F4.wireOp",EDGE,"E142.2.0"),sQuery(id+"F4.wireOp",EDGE,"E142.2.1"),sQuery(id+"F4.wireOp",EDGE,"E142.2.2"),sQuery(id+"F4.wireOp",EDGE,"E142.2.3"),sQuery(id+"F4.wireOp",EDGE,"E142.2.4"),sQuery(id+"F4.wireOp",EDGE,"E142.2.5"),sQuery(id+"F4.wireOp",EDGE,"E142.3.0"),sQuery(id+"F4.wireOp",EDGE,"E142.3.1"),sQuery(id+"F4.wireOp",EDGE,"E142.3.2"),sQuery(id+"F4.wireOp",EDGE,"E142.3.3"),sQuery(id+"F4.wireOp",EDGE,"E142.3.4"),sQuery(id+"F4.wireOp",EDGE,"E142.3.5"),sQuery(id+"F4.wireOp",EDGE,"E142.4.0"),sQuery(id+"F4.wireOp",EDGE,"E142.4.1"),sQuery(id+"F4.wireOp",EDGE,"E142.4.2"),sQuery(id+"F4.wireOp",EDGE,"E142.4.3"),sQuery(id+"F4.wireOp",EDGE,"E142.4.4"),sQuery(id+"F4.wireOp",EDGE,"E142.4.5"),sQuery(id+"F4.wireOp",EDGE,"E142.5.0"),sQuery(id+"F4.wireOp",EDGE,"E142.5.1"),sQuery(id+"F4.wireOp",EDGE,"E142.5.2"),sQuery(id+"F4.wireOp",EDGE,"E142.5.3"),sQuery(id+"F4.wireOp",EDGE,"E142.5.4"),sQuery(id+"F4.wireOp",EDGE,"E142.5.5"),sQuery(id+"F4.wireOp",EDGE,"E143"),sQuery(id+"F4.wireOp",EDGE,"E144.1.0"),sQuery(id+"F4.wireOp",EDGE,"E144.1.1"),sQuery(id+"F4.wireOp",EDGE,"E144.1.2"),sQuery(id+"F4.wireOp",EDGE,"E144.2.0"),sQuery(id+"F4.wireOp",EDGE,"E144.2.1"),sQuery(id+"F4.wireOp",EDGE,"E144.2.2"),sQuery(id+"F4.wireOp",EDGE,"E144.3.0"),sQuery(id+"F4.wireOp",EDGE,"E144.3.1"),sQuery(id+"F4.wireOp",EDGE,"E144.3.2"),sQuery(id+"F4.wireOp",EDGE,"E144.4.0"),sQuery(id+"F4.wireOp",EDGE,"E144.4.1"),sQuery(id+"F4.wireOp",EDGE,"E144.4.2"),sQuery(id+"F4.wireOp",EDGE,"E144.5.0"),sQuery(id+"F4.wireOp",EDGE,"E144.5.1"),sQuery(id+"F4.wireOp",EDGE,"E144.5.2"),sQuery(id+"F4.wireOp",EDGE,"E146"),sQuery(id+"F4.wireOp",EDGE,"E148.1.0"),sQuery(id+"F4.wireOp",EDGE,"E148.1.1"),sQuery(id+"F4.wireOp",EDGE,"E148.1.2"),sQuery(id+"F4.wireOp",EDGE,"E148.1.3"),sQuery(id+"F4.wireOp",EDGE,"E148.1.4"),sQuery(id+"F4.wireOp",EDGE,"E148.1.5"),sQuery(id+"F4.wireOp",EDGE,"E148.2.0"),sQuery(id+"F4.wireOp",EDGE,"E148.2.1"),sQuery(id+"F4.wireOp",EDGE,"E148.2.2"),sQuery(id+"F4.wireOp",EDGE,"E148.2.3"),sQuery(id+"F4.wireOp",EDGE,"E148.2.4"),sQuery(id+"F4.wireOp",EDGE,"E148.2.5"),sQuery(id+"F4.wireOp",EDGE,"E148.3.0"),sQuery(id+"F4.wireOp",EDGE,"E148.3.1"),sQuery(id+"F4.wireOp",EDGE,"E148.3.2"),sQuery(id+"F4.wireOp",EDGE,"E148.3.3"),sQuery(id+"F4.wireOp",EDGE,"E148.3.4"),sQuery(id+"F4.wireOp",EDGE,"E148.3.5"),sQuery(id+"F4.wireOp",EDGE,"E148.4.0"),sQuery(id+"F4.wireOp",EDGE,"E148.4.1"),sQuery(id+"F4.wireOp",EDGE,"E148.4.2"),sQuery(id+"F4.wireOp",EDGE,"E148.4.3"),sQuery(id+"F4.wireOp",EDGE,"E148.4.4"),sQuery(id+"F4.wireOp",EDGE,"E148.4.5"),sQuery(id+"F4.wireOp",EDGE,"E148.5.0"),sQuery(id+"F4.wireOp",EDGE,"E148.5.1"),sQuery(id+"F4.wireOp",EDGE,"E148.5.2"),sQuery(id+"F4.wireOp",EDGE,"E148.5.3"),sQuery(id+"F4.wireOp",EDGE,"E148.5.4"),sQuery(id+"F4.wireOp",EDGE,"E148.5.5")])]});
            var Q4;
            Q4=sQuery(id+"F0.wireOp",VERTEX,"E80");
            var Q5;
            Q5=sQuery(id+"F0.wireOp",VERTEX,"E79");
            transform(context, id + "F8", {"entities" : qUnion([Q0, Q1, Q2, Q3]), "transformType" : TransformType.TRANSLATION_ENTITY, "oppositeDirectionEntity" : false, "transformLine" : qUnion([Q4, Q5]), "makeCopy" : true});
        }
        {
            var Q0;
            Q0=qCreatedBy(makeId("Right.planeOp"),FACE);
            var sketch = newSketch(context, id + "F9", { "sketchPlane" : qUnion([Q0])});
            skArc(sketch, "E150", {"start": v(305.4, 206.2) * mm, "mid": v(172.93, 325.4) * mm, "end": v(0, 368.5) * mm});
            skPoint(sketch, "E151.0", {"position": v(-220.92, -262.68) * mm});
            skArc(sketch, "E152", {"start": v(284.46, 192.06) * mm, "mid": v(-229.58, 255.15) * mm, "end": v(-220.92, -262.68) * mm, "construction": true});
            skLineSegment(sketch, "E153", {"start": v(305.4, 206.2) * mm, "end": v(284.46, 192.06) * mm, "construction": true});
            skLineSegment(sketch, "E154", {"start": v(0, 368.5) * mm, "end": v(0, 0) * mm, "construction": true});
            skArc(sketch, "E155", {"start": v(0, 368.5) * mm, "mid": v(-346.2, 126.23) * mm, "end": v(-237.19, -282.02) * mm});
            skArc(sketch, "E156", {"start": v(-237.19, -282.02) * mm, "mid": v(-231.07, -263.83) * mm, "end": v(-239, -246.35) * mm});
            skLineSegment(sketch, "E157", {"start": v(-220.92, -262.68) * mm, "end": v(-237.19, -282.02) * mm, "construction": true});
            skArc(sketch, "E158", {"start": v(-24.34, 342.37) * mm, "mid": v(-7.03, 350.64) * mm, "end": v(0, 368.5) * mm});
            skArc(sketch, "E159", {"start": v(270.13, 211.75) * mm, "mid": v(286.67, 202.03) * mm, "end": v(305.4, 206.2) * mm});
            skLineSegment(sketch, "E160", {"start": v(305.4, 206.2) * mm, "end": v(284.46, 192.06) * mm});
            skLineSegment(sketch, "E161", {"start": v(270.13, 211.75) * mm, "end": v(284.46, 192.06) * mm});
            skLineSegment(sketch, "E162", {"start": v(0, 368.5) * mm, "end": v(0, 343.23) * mm});
            skLineSegment(sketch, "E163", {"start": v(0, 343.23) * mm, "end": v(-24.34, 342.37) * mm});
            skLineSegment(sketch, "E164", {"start": v(-239, -246.35) * mm, "end": v(-220.92, -262.68) * mm});
            skLineSegment(sketch, "E165", {"start": v(-220.92, -262.68) * mm, "end": v(-237.19, -282.02) * mm});
            skArc(sketch, "E166", {"start": v(0, -359) * mm, "mid": v(359, 0) * mm, "end": v(0, 359) * mm, "construction": true});
            skLineSegment(sketch, "E167", {"start": v(0, 0) * mm, "end": v(0, -359) * mm, "construction": true});
            skSolve(sketch);
        }
        {
            var Q0;
            Q0=qCreatedBy(makeId("Right.planeOp"),FACE);
            var Q1;
            Q1=sQuery(id+"F0.wireOp",VERTEX,"E53.0.end");
            cPlane(context, id + "F10", {"entities" : qUnion([Q0, Q1]), "cplaneType" : CPlaneType.PLANE_POINT, "offset" : 25 * mm, "width" : 150 * mm, "height" : 150 * mm});
        }
        {
            var Q0;
            Q0=qCreatedBy(id+"F10.planeOp",FACE);
            var sketch = newSketch(context, id + "F11", { "sketchPlane" : qUnion([Q0])});
            skArc(sketch, "E168", {"start": v(303.38, 196.58) * mm, "mid": v(172.65, 317.6) * mm, "end": v(0, 361.5) * mm});
            skPoint(sketch, "E169.0", {"position": v(-207.1, -271.32) * mm});
            skArc(sketch, "E170", {"start": v(286.45, 185.6) * mm, "mid": v(-231.88, 250.47) * mm, "end": v(-207.1, -271.32) * mm, "construction": true});
            skLineSegment(sketch, "E171", {"start": v(303.38, 196.58) * mm, "end": v(286.45, 185.6) * mm, "construction": true});
            skLineSegment(sketch, "E172", {"start": v(0, 361.5) * mm, "end": v(0, 0) * mm, "construction": true});
            skArc(sketch, "E173", {"start": v(0, 361.5) * mm, "mid": v(-342.46, 115.77) * mm, "end": v(-219.34, -287.35) * mm});
            skArc(sketch, "E174", {"start": v(-219.34, -287.35) * mm, "mid": v(-215.2, -272.58) * mm, "end": v(-222.32, -258.99) * mm});
            skLineSegment(sketch, "E175", {"start": v(-207.1, -271.32) * mm, "end": v(-219.34, -287.35) * mm, "construction": true});
            skArc(sketch, "E176", {"start": v(-19.58, 340.76) * mm, "mid": v(-5.67, 347.24) * mm, "end": v(0, 361.5) * mm});
            skArc(sketch, "E177", {"start": v(275.33, 201.74) * mm, "mid": v(288.33, 193.58) * mm, "end": v(303.38, 196.58) * mm});
            skLineSegment(sketch, "E178", {"start": v(303.38, 196.58) * mm, "end": v(286.45, 185.6) * mm});
            skLineSegment(sketch, "E179", {"start": v(275.33, 201.74) * mm, "end": v(286.45, 185.6) * mm});
            skLineSegment(sketch, "E180", {"start": v(0, 361.5) * mm, "end": v(0, 341.32) * mm});
            skLineSegment(sketch, "E181", {"start": v(0, 341.32) * mm, "end": v(-19.58, 340.76) * mm});
            skLineSegment(sketch, "E182", {"start": v(-222.32, -258.99) * mm, "end": v(-207.1, -271.32) * mm});
            skLineSegment(sketch, "E183", {"start": v(-207.1, -271.32) * mm, "end": v(-219.34, -287.35) * mm});
            skPoint(sketch, "E184.0", {"position": v(0, 352) * mm});
            skArc(sketch, "E185", {"start": v(0, -352) * mm, "mid": v(352, 0) * mm, "end": v(0, 352) * mm, "construction": true});
            skLineSegment(sketch, "E186", {"start": v(0, -352) * mm, "end": v(0, 0) * mm, "construction": true});
            skSolve(sketch);
        }
        {
            var Q0;
            Q0=makeQuery(id+"F0.imprint","IMPRINT",FACE,{"disambiguationData":[TD([[makeQuery(id+"F0.imprint","IMPRINT",EDGE,{"derivedFrom":sQuery(id+"F0.wireOp",EDGE,"E37")}),-1.0]])]});
            var Q1;
            Q1=makeQuery(id+"F0.imprint","IMPRINT",FACE,{"disambiguationData":[TD([[makeQuery(id+"F0.imprint","IMPRINT",EDGE,{"derivedFrom":sQuery(id+"F0.wireOp",EDGE,"E77.1.0.1")}),1.0]])]});
            var Q2;
            Q2=sQuery(id+"F9.wireOp",EDGE,"E155");
            sweep(context, id + "F12", {"profiles" : qUnion([Q0, Q1]), "path" : qUnion([Q2])});
        }
        {
            var Q0;
            Q0=makeQuery(id+"F0.imprint","IMPRINT",FACE,{"disambiguationData":[TD([[makeQuery(id+"F0.imprint","IMPRINT",EDGE,{"derivedFrom":sQuery(id+"F0.wireOp",EDGE,"E77.1.0.1")}),1.0]])]});
            var Q1;
            Q1=sQuery(id+"F9.wireOp",EDGE,"E150");
            sweep(context, id + "F13", {"operationType" : NewBodyOperationType.ADD, "profiles" : qUnion([Q0]), "path" : qUnion([Q1])});
        }
        {
            var Q0;
            Q0=makeQuery(id+"F0.imprint","IMPRINT",FACE,{"disambiguationData":[TD([[makeQuery(id+"F0.imprint","IMPRINT",EDGE,{"derivedFrom":sQuery(id+"F0.wireOp",EDGE,"E71")}),-1.0]])]});
            var Q1;
            Q1=makeQuery(id+"F0.imprint","IMPRINT",FACE,{"disambiguationData":[TD([[makeQuery(id+"F0.imprint","IMPRINT",EDGE,{"derivedFrom":sQuery(id+"F0.wireOp",EDGE,"E78.1.0.0")}),-1.0]])]});
            var Q2;
            Q2=sQuery(id+"F11.wireOp",EDGE,"E173");
            sweep(context, id + "F14", {"profiles" : qUnion([Q0, Q1]), "path" : qUnion([Q2])});
        }
        {
            var Q0;
            Q0=makeQuery(id+"F0.imprint","IMPRINT",FACE,{"disambiguationData":[TD([[makeQuery(id+"F0.imprint","IMPRINT",EDGE,{"derivedFrom":sQuery(id+"F0.wireOp",EDGE,"E78.1.0.0")}),-1.0]])]});
            var Q1;
            Q1=sQuery(id+"F11.wireOp",EDGE,"E168");
            sweep(context, id + "F15", {"operationType" : NewBodyOperationType.ADD, "profiles" : qUnion([Q0]), "path" : qUnion([Q1])});
        }
        {
            var Q0;
            Q0=makeQuery(id+"F9.imprint","IMPRINT",FACE,{"disambiguationData":[TD([[makeQuery(id+"F9.imprint","IMPRINT",EDGE,{"derivedFrom":sQuery(id+"F9.wireOp",EDGE,"E156")}),-1.0]])]});
            var Q1;
            Q1=makeQuery(id+"F9.imprint","IMPRINT",FACE,{"disambiguationData":[TD([[makeQuery(id+"F9.imprint","IMPRINT",EDGE,{"derivedFrom":sQuery(id+"F9.wireOp",EDGE,"E159")}),-1.0]])]});
            extrude(context, id + "F16", {"entities" : qUnion([Q0, Q1]), "operationType" : NewBodyOperationType.REMOVE, "endBound" : BoundingType.THROUGH_ALL, "oppositeDirection" : true, "depth" : 25 * mm, "hasSecondDirection" : true, "secondDirectionBound" : SecondDirectionBoundingType.THROUGH_ALL, "secondDirectionOppositeDirection" : false, "secondDirectionDepth" : 25 * mm});
        }
        {
            var Q0;
            Q0=makeQuery(id+"F9.imprint","IMPRINT",FACE,{"disambiguationData":[TD([[makeQuery(id+"F9.imprint","IMPRINT",EDGE,{"derivedFrom":sQuery(id+"F9.wireOp",EDGE,"E158")}),-1.0]])]});
            extrude(context, id + "F17", {"entities" : qUnion([Q0]), "operationType" : NewBodyOperationType.REMOVE, "endBound" : BoundingType.THROUGH_ALL, "oppositeDirection" : true, "depth" : 25 * mm, "hasSecondDirection" : true, "secondDirectionBound" : SecondDirectionBoundingType.THROUGH_ALL, "secondDirectionOppositeDirection" : false, "secondDirectionDepth" : 25 * mm});
        }
        {
            var Q0;
            Q0=makeQuery(id+"F11.imprint","IMPRINT",FACE,{"disambiguationData":[TD([[makeQuery(id+"F11.imprint","IMPRINT",EDGE,{"derivedFrom":sQuery(id+"F11.wireOp",EDGE,"E177")}),-1.0]])]});
            var Q1;
            Q1=makeQuery(id+"F11.imprint","IMPRINT",FACE,{"disambiguationData":[TD([[makeQuery(id+"F11.imprint","IMPRINT",EDGE,{"derivedFrom":sQuery(id+"F11.wireOp",EDGE,"E174")}),-1.0]])]});
            extrude(context, id + "F18", {"entities" : qUnion([Q0, Q1]), "operationType" : NewBodyOperationType.REMOVE, "endBound" : BoundingType.THROUGH_ALL, "oppositeDirection" : true, "depth" : 25 * mm, "hasSecondDirection" : true, "secondDirectionBound" : SecondDirectionBoundingType.THROUGH_ALL, "secondDirectionOppositeDirection" : false, "secondDirectionDepth" : 25 * mm});
        }
        {
            var Q0;
            Q0=makeQuery(id+"F11.imprint","IMPRINT",FACE,{"disambiguationData":[TD([[makeQuery(id+"F11.imprint","IMPRINT",EDGE,{"derivedFrom":sQuery(id+"F11.wireOp",EDGE,"E176")}),-1.0]])]});
            extrude(context, id + "F19", {"entities" : qUnion([Q0]), "operationType" : NewBodyOperationType.REMOVE, "endBound" : BoundingType.THROUGH_ALL, "depth" : 25 * mm, "hasSecondDirection" : true, "secondDirectionBound" : SecondDirectionBoundingType.THROUGH_ALL, "secondDirectionOppositeDirection" : true, "secondDirectionDepth" : 25 * mm});
        }
    });
